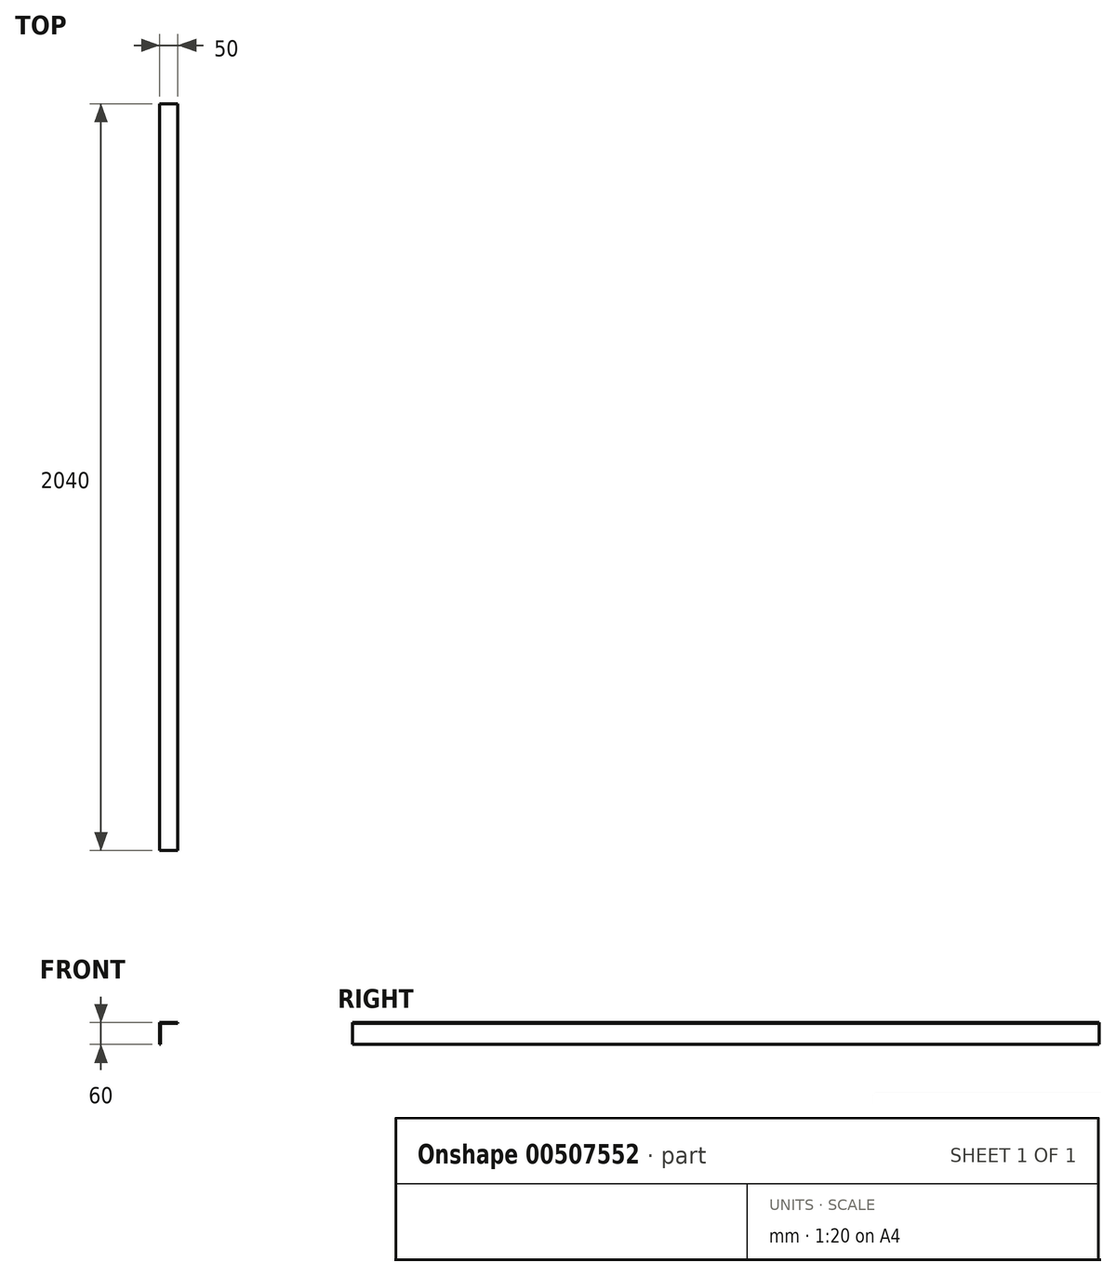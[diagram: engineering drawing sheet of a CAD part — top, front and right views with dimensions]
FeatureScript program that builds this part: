
annotation { "Feature Type Name" : "Feature", "Feature Type Description" : "" }
export const myFeature = defineFeature(function(context is Context, id is Id, definition is map)
    precondition{}
    {
        {
            var Q0;
            Q0=qCreatedBy(makeId("Front.planeOp"),FACE);
            var sketch = newSketch(context, id + "F0", { "sketchPlane" : qUnion([Q0])});
            skLineSegment(sketch, "E0", {"start": v(0, 0) * mm, "end": v(0, 60) * mm});
            skLineSegment(sketch, "E1", {"start": v(0, 60) * mm, "end": v(50, 60) * mm});
            skLineSegment(sketch, "E2", {"start": v(50, 60) * mm, "end": v(50, 58) * mm});
            skLineSegment(sketch, "E3", {"start": v(50, 58) * mm, "end": v(2, 58) * mm});
            skLineSegment(sketch, "E4", {"start": v(2, 58) * mm, "end": v(2, 0) * mm});
            skLineSegment(sketch, "E5", {"start": v(2, 0) * mm, "end": v(0, 0) * mm});
            skSolve(sketch);
        }
        {
            var Q0;
            Q0 = qSketchRegion(id + "F0", true);
            extrude(context, id + "F1", {"entities" : qUnion([Q0]), "depth" : 2040 * mm, "offsetDistance" : 25 * mm});
        }
    });
